# Revit family: Thorn ALUMET CD
name_source: partatom
category: Lighting Fixtures
revit_build: Autodesk Revit 2016 (Build: 20150220_1215(x64)
units: mm (PartAtom-declared; Revit-internal decimal feet)

## family parameters
Always vertical = Yes
Cut with Voids When Loaded = No
Light Source = Yes
OmniClass Number = 23.80.70.00
OmniClass Title = Lighting
Part Type = Normal
Room Calculation Point = No
Round Connector Dimension = Use Diameter
Shared = No
Work Plane-Based = No

## types (4) — shared parameters
Color Filter = 16777215
Description = LED Amenity lighting lantern
Dimming Lamp Color Temperature Shift = <None>
Lamp = LED
Manufacturer = Thorn Lighting
Tilt Angle = 60.00°
Voltage = 230 V

## per-type parameters (varying)
| type | Apparent Load | Model | Photometric Web File | URL |
| ALUMET CD R/S | 21 VA | 96274723 | TLLA_ALCD18L35RSPR3KG33_DC.IES | www.thornlighting.com/96274723 |
| ALUMET CD NR-A | 114 VA | 96274734 | TLLA_ALCD24L25NR3KG33_DC.IES | www.thornlighting.com/96274734 |
| ALUMET CD RWETS | 20 VA | 96274766 | TLLA_ALCD24L25RWETS3KG33_DC.IES | www.thornlighting.com/96274766 |
| ALUMET CD WSC-A | 20 VA | 96274740 | TLLA_ALCD24L25WSC3KG33_DC.IES | www.thornlighting.com/96274740 |

## geometry (parser evidence)
native form markers: Sweep x2
no freeform markers — native parametric forms only
